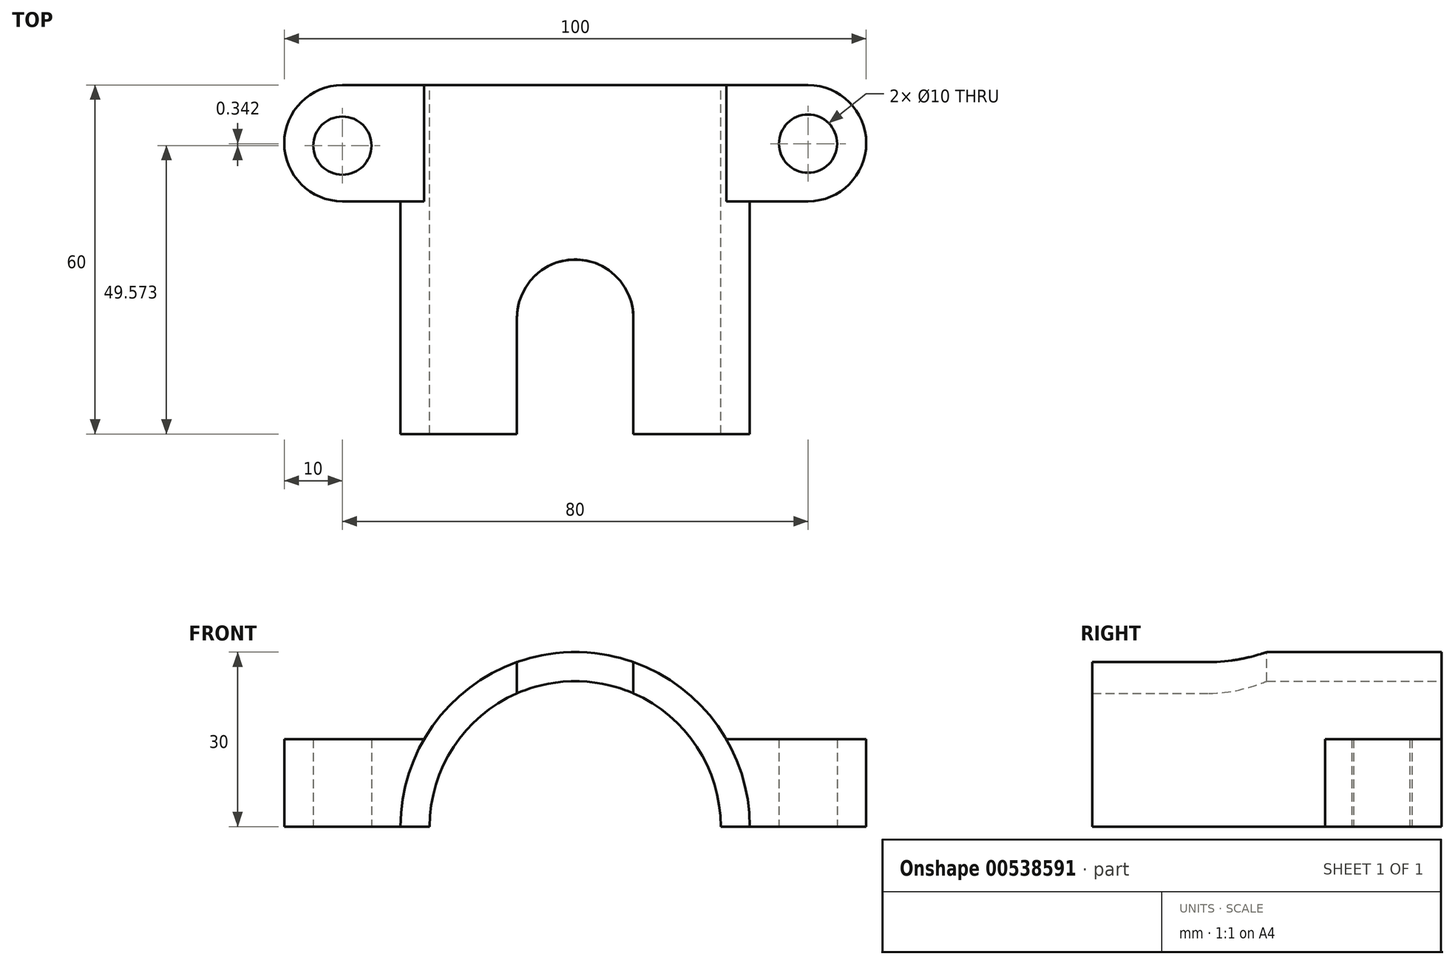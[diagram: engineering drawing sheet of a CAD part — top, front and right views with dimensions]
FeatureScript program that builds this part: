
annotation { "Feature Type Name" : "Feature", "Feature Type Description" : "" }
export const myFeature = defineFeature(function(context is Context, id is Id, definition is map)
    precondition{}
    {
        {
            assignVariable(context, id + "F0", {"name" : "A", "anyValue" : 15});
        }
        {
            var Q0;
            Q0=qCreatedBy(makeId("Front.planeOp"),FACE);
            var sketch = newSketch(context, id + "F1", { "sketchPlane" : qUnion([Q0])});
            skArc(sketch, "E0", {"start": v(-30, 0) * mm, "mid": v(0, 30) * mm, "end": v(30, 0) * mm});
            skLineSegment(sketch, "E1", {"start": v(-30, 0) * mm, "end": v(30, 0) * mm});
            skSolve(sketch);
        }
        {
            var Q0;
            Q0=qSketchRegion(id+"F1",true);
            extrude(context, id + "F2", {"entities" : qUnion([Q0]), "depth" : 60 * mm, "offsetDistance" : 25 * mm});
        }
        {
            var Q0;
            Q0=qCreatedBy(makeId("Top.planeOp"),FACE);
            var sketch = newSketch(context, id + "F3", { "sketchPlane" : qUnion([Q0])});
            skLineSegment(sketch, "E2", {"start": v(-40, 0) * mm, "end": v(40, 0) * mm});
            skLineSegment(sketch, "E3", {"start": v(-80, -10) * mm, "end": v(90, -10) * mm, "construction": true});
            skLineSegment(sketch, "E4.MirrorCS", {"start": v(-40, -20) * mm, "end": v(40, -20) * mm});
            skArc(sketch, "E5", {"start": v(-40, 0) * mm, "mid": v(-50, -10) * mm, "end": v(-40, -20) * mm});
            skArc(sketch, "E6", {"start": v(40, -20) * mm, "mid": v(50, -10) * mm, "end": v(40, 0) * mm});
            skSolve(sketch);
        }
        {
            var Q0;
            Q0=qSketchRegion(id+"F3",true);
            extrude(context, id + "F4", {"entities" : qUnion([Q0]), "operationType" : NewBodyOperationType.ADD, "depth" : (getVariable(context, 'A')) * mm, "offsetDistance" : 25 * mm});
        }
        {
            var Q0;
            Q0=qCreatedBy(makeId("Front.planeOp"),FACE);
            var sketch = newSketch(context, id + "F5", { "sketchPlane" : qUnion([Q0])});
            skArc(sketch, "E7", {"start": v(-25, 0) * mm, "mid": v(0, 25) * mm, "end": v(25, 0) * mm});
            skLineSegment(sketch, "E8", {"start": v(25, 0) * mm, "end": v(-25, 0) * mm});
            skSolve(sketch);
        }
        {
            var Q0;
            Q0=qSketchRegion(id+"F5",true);
            extrude(context, id + "F6", {"entities" : qUnion([Q0]), "operationType" : NewBodyOperationType.REMOVE, "endBound" : BoundingType.THROUGH_ALL, "depth" : 25 * mm, "offsetDistance" : 25 * mm});
        }
        {
            var Q0;
            Q0=qCreatedBy(makeId("Top.planeOp"),FACE);
            cPlane(context, id + "F7", {"entities" : qUnion([Q0]), "cplaneType" : CPlaneType.OFFSET, "offset" : 30 * mm, "width" : 150 * mm, "height" : 150 * mm});
        }
        {
            var Q0;
            Q0=qCreatedBy(id+"F7.planeOp",FACE);
            var sketch = newSketch(context, id + "F8", { "sketchPlane" : qUnion([Q0])});
            skPoint(sketch, "E9", {"position": v(0, -60) * mm});
            skLineSegment(sketch, "E10", {"start": v(0, -60) * mm, "end": v(10, -60) * mm});
            skLineSegment(sketch, "E11", {"start": v(10, -60) * mm, "end": v(0, -60) * mm});
            skLineSegment(sketch, "E12", {"start": v(0, 0) * mm, "end": v(0, -65.4) * mm, "construction": true});
            skLineSegment(sketch, "E13.MirrorCS", {"start": v(-10, -60) * mm, "end": v(0, -60) * mm});
            skLineSegment(sketch, "E14", {"start": v(-10, -60) * mm, "end": v(-10, -40) * mm});
            skLineSegment(sketch, "E15.MirrorCS", {"start": v(10, -60) * mm, "end": v(10, -40) * mm});
            skArc(sketch, "E16", {"start": v(10, -40) * mm, "mid": v(0, -30) * mm, "end": v(-10, -40) * mm});
            skSolve(sketch);
        }
        {
            var Q0;
            Q0=qSketchRegion(id+"F8",true);
            extrude(context, id + "F9", {"entities" : qUnion([Q0]), "operationType" : NewBodyOperationType.REMOVE, "endBound" : BoundingType.THROUGH_ALL, "oppositeDirection" : true, "depth" : 25 * mm, "offsetDistance" : 25 * mm});
        }
        {
            var Q0;
            Q0=qCreatedBy(makeId("Top.planeOp"),FACE);
            var sketch = newSketch(context, id + "F10", { "sketchPlane" : qUnion([Q0])});
            skLineSegment(sketch, "E17", {"start": v(0, 0) * mm, "end": v(0, -67.35) * mm, "construction": true});
            skCircle(sketch, "E18", {"center": v(-40, -10.43) * mm, "radius": 5 * mm});
            skCircle(sketch, "E19", {"center": v(40, -10.09) * mm, "radius": 5 * mm});
            skSolve(sketch);
        }
        {
            var Q0;
            Q0=qSketchRegion(id+"F10",true);
            extrude(context, id + "F11", {"entities" : qUnion([Q0]), "operationType" : NewBodyOperationType.REMOVE, "endBound" : BoundingType.UP_TO_NEXT, "depth" : 25 * mm, "offsetDistance" : 25 * mm});
        }
    });
